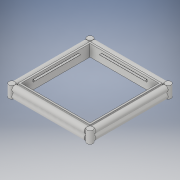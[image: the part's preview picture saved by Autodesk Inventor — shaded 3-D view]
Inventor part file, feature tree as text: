
AUTODESK INVENTOR PART (.ipt)
format: ipt  version: 2018 (Build 220112000, 112)  size: 329,728 bytes
history: native  units: in
note: dims shown in document units (in); Inventor stores cm internally (conversion verified against a paired STEP export)
features: extrude x17, sketch x17
ambient origin geometry x8: Origin, YZ Plane, XZ Plane, XY Plane, X Axis, Y Axis, Z Axis, Center Point
bodies: Solid1 (feature_tree)
feature tree (34):
  extrude  "Extrusion1"  Depth=0.745in
  extrude  "Extrusion2"  Depth=0.745in
  extrude  "Extrusion3"  Depth=0.745in
  extrude  "Extrusion4"  Depth=0.745in
  extrude  "Extrusion7"  Depth=30.0in TaperAngle=0.0deg
  extrude  "Extrusion8"  Depth=5.0in
  extrude  "Extrusion9"  Depth=1.25in
  extrude  "Extrusion10"  Depth=1.25in
  extrude  "Extrusion11"  Depth=30.745in TaperAngle=0.0deg
  extrude  "Extrusion15"  Depth=2.5in
  extrude  "Extrusion16"  Depth=1.25in
  extrude  "Extrusion19"  Depth=1.25in
  extrude  "Extrusion22"  Depth=30.745in TaperAngle=0.0deg
  extrude  "Extrusion23"  Depth=2.5in
  extrude  "Extrusion24"  Depth=1.25in
  sketch  "Sketch1"  dims[d0=5.0in d1=0.745in]
  sketch  "Sketch2"  dims[d2=30.0in d3=0.0in d4=0.745in]
  sketch  "Sketch3"  dims[d5=30.0in d6=0.0in d8=0.745in]
  sketch  "Sketch4"  dims[d9=30.0in d10=0.0in d11=0.745in]
  sketch  "Sketch8"  dims[d12=0.0in d13=30.0in d14=0.0in]
  sketch  "Sketch10"  dims[d21=5.0in d32=2.5in]
  sketch  "Sketch12"  dims[d33=2.5in d35=1.25in]
  sketch  "Sketch13"  dims[d36=1.25in d37=1.25in]
  sketch  "Sketch14"  dims[d38=1.25in d39=30.745in d40=0.0in]
  sketch  "Sketch15"  dims[d41=2.5in d42=2.5in]
  sketch  "Sketch17"  dims[d43=1.25in d44=1.25in]
  sketch  "Sketch20"  dims[d45=1.25in d46=1.25in]
  sketch  "Sketch23"  dims[d52=1.25in d53=1.25in]
  sketch  "Sketch24"  dims[d54=1.25in d55=1.25in]
  sketch  "Sketch26"  dims[d56=30.745in d57=0.0in d58=2.5in d59=2.5in d64=2.5in d65=1.25in d66=1.25in d67=1.25in d68=30.745in d69=0.0in d70=1.25in d71=2.5in d72=1.25in d73=2.5in d74=1.25in d75=1.25in d76=2.5in d77=1.25in d78=1.25in d79=2.5in d80=1.25in d81=1.25in d82=5.0in d83=0.0in d99=1.0in d100=2.9in d101=5.0in d102=5.0in d103=0.065in d104=0.0in d105=0.065in d106=0.935in d107=0.0in d115=1.0in d116=2.9in d117=5.0in d118=19.255in d119=5.0in d120=0.065in d121=0.0in d122=5.0in d123=1.0in d124=2.9in d125=19.255in d127=0.0in d128=0.065in d129=5.0in d130=5.0in d131=1.0in d132=2.9in d133=19.255in d135=0.0in d136=0.065in d137=5.0in d138=0.065in d139=0.935in d140=0.0in d141=0.065in d142=0.935in d143=0.0in d144=0.065in d145=0.935in d146=0.0in]
  sketch  "Sketch21"  dims[d47=1.25in d48=30.745in d49=0.0in]
  sketch  "Sketch22"  dims[d50=2.5in d51=2.5in]
  extrude  "Extrusion20"  Depth=1.25in
  extrude  "Extrusion21"  Depth=0.935in
